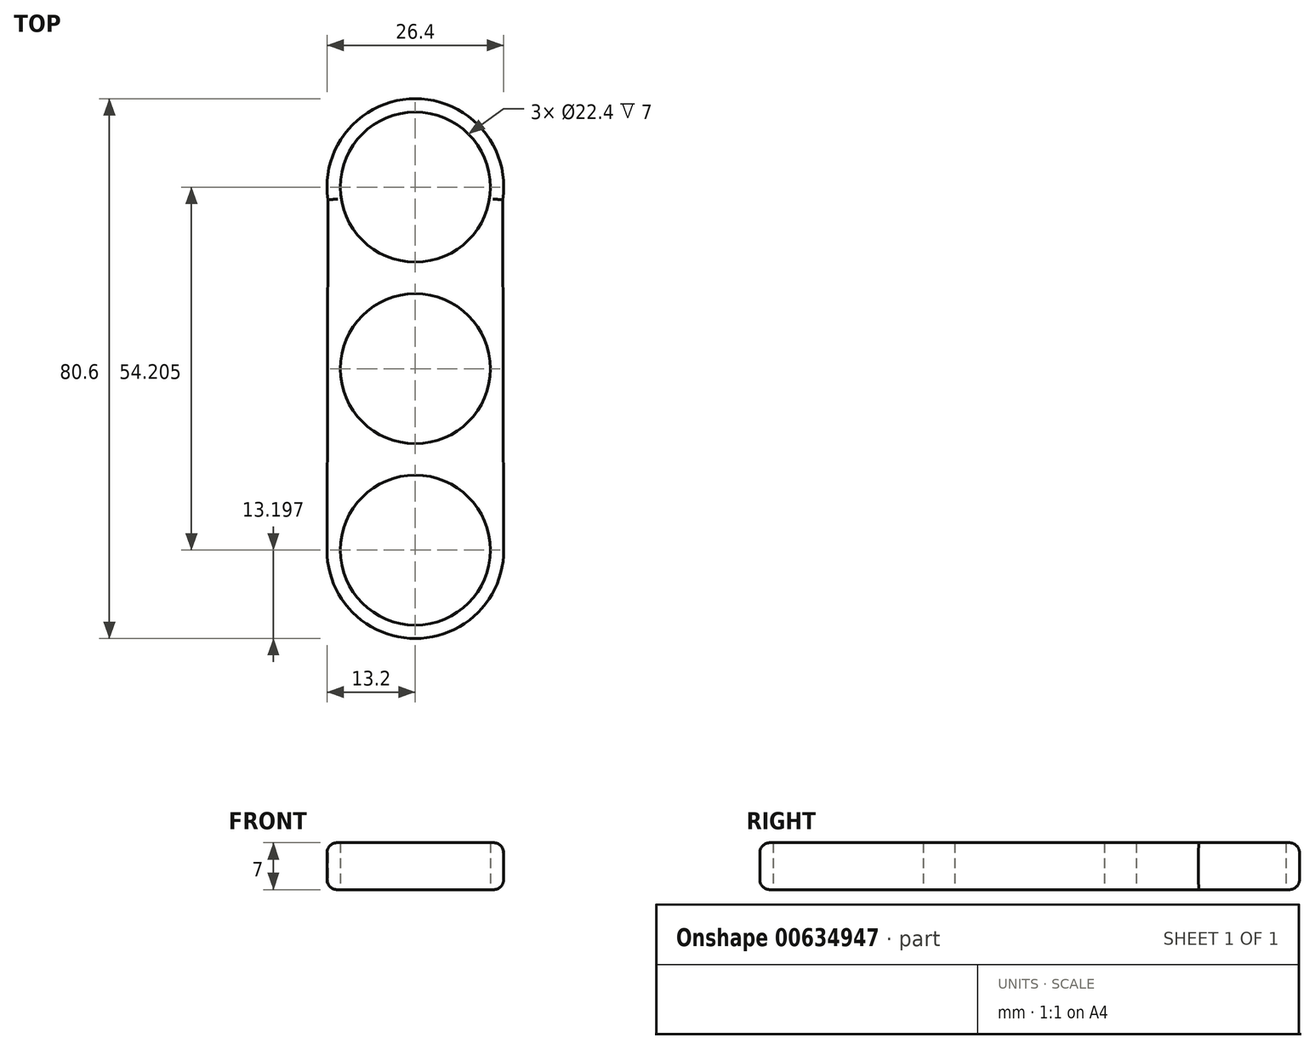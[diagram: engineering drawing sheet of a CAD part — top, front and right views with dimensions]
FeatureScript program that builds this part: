
annotation { "Feature Type Name" : "Feature", "Feature Type Description" : "" }
export const myFeature = defineFeature(function(context is Context, id is Id, definition is map)
    precondition{}
    {
        {
            var Q0;
            Q0=qCreatedBy(makeId("Top.planeOp"),FACE);
            var sketch = newSketch(context, id + "F0", { "sketchPlane" : qUnion([Q0])});
            skCircle(sketch, "E0", {"center": v(0, 0) * mm, "radius": 11.2 * mm});
            skArc(sketch, "E1", {"start": v(13.13, -1.33) * mm, "mid": v(13.2, 0.03) * mm, "end": v(13.13, 1.4) * mm});
            skCircle(sketch, "E2", {"center": v(0, 27.12) * mm, "radius": 11.2 * mm});
            skArc(sketch, "E3", {"start": v(13.06, 25.23) * mm, "mid": v(0, 40.32) * mm, "end": v(-13.06, 25.23) * mm});
            skCircle(sketch, "E4.1.0", {"center": v(0, -27.08) * mm, "radius": 11.2 * mm});
            skArc(sketch, "E4.1.1", {"start": v(-13.2, -27.05) * mm, "mid": v(0, -40.28) * mm, "end": v(13.2, -27.05) * mm});
            skPoint(sketch, "E4.center", {"position": v(0, 0.02) * mm});
            skLineSegment(sketch, "E5", {"start": v(13.06, 25.23) * mm, "end": v(13.2, -27.05) * mm});
            skLineSegment(sketch, "E6", {"start": v(-13.06, 25.23) * mm, "end": v(-13.2, -27.05) * mm});
            skArc(sketch, "E7.trimOffspring", {"start": v(-13.13, 1.4) * mm, "mid": v(-13.2, 0.03) * mm, "end": v(-13.13, -1.33) * mm});
            skSolve(sketch);
        }
        {
            var Q0;
            Q0=qCreatedBy(makeId("Top.planeOp"),FACE);
            var sketch = newSketch(context, id + "F1", { "sketchPlane" : qUnion([Q0])});
            skSolve(sketch);
        }
        {
            var Q0;
            Q0 = qSketchRegion(id + "F1", true);
            var Q1;
            Q1=makeQuery(id+"F0.imprint","IMPRINT",FACE,{"disambiguationData":[TD([[makeQuery(id+"F0.imprint","IMPRINT",EDGE,{"derivedFrom":sQuery(id+"F0.wireOp",EDGE,"E0")}),-1.0]])]});
            extrude(context, id + "F2", {"entities" : qUnion([Q0, Q1]), "depth" : 7 * mm, "offsetDistance" : 25 * mm});
        }
        {
            var Q0;
            Q0=makeQuery(id+"F2.opExtrude","CAP_EDGE",EDGE,{"disambiguationData":[OSD([sQuery(id+"F0.wireOp",EDGE,"E5")])],"isStart":false});
            var Q1;
            Q1=makeQuery(id+"F2.opExtrude","CAP_EDGE",EDGE,{"disambiguationData":[OSD([sQuery(id+"F0.wireOp",EDGE,"E4.1.1")])],"isStart":false});
            var Q2;
            Q2=makeQuery(id+"F2.opExtrude","CAP_EDGE",EDGE,{"disambiguationData":[OSD([sQuery(id+"F0.wireOp",EDGE,"E6")])],"isStart":false});
            var Q3;
            Q3=makeQuery(id+"F2.opExtrude","CAP_EDGE",EDGE,{"disambiguationData":[OSD([sQuery(id+"F0.wireOp",EDGE,"E3")])],"isStart":false});
            fillet(context, id + "F3", {"entities" : qUnion([Q0, Q1, Q2, Q3]), "radius" : 1.5 * mm, "tangentPropagation" : true, "allowEdgeOverflow" : false});
        }
        {
            var Q0;
            Q0=makeQuery(id+"F2.opExtrude","CAP_EDGE",EDGE,{"disambiguationData":[OSD([sQuery(id+"F0.wireOp",EDGE,"E3")])],"isStart":true});
            var Q1;
            Q1=makeQuery(id+"F2.opExtrude","CAP_EDGE",EDGE,{"disambiguationData":[OSD([sQuery(id+"F0.wireOp",EDGE,"E5")])],"isStart":true});
            var Q2;
            Q2=makeQuery(id+"F2.opExtrude","CAP_EDGE",EDGE,{"disambiguationData":[OSD([sQuery(id+"F0.wireOp",EDGE,"E6")])],"isStart":true});
            var Q3;
            Q3=makeQuery(id+"F2.opExtrude","CAP_EDGE",EDGE,{"disambiguationData":[OSD([sQuery(id+"F0.wireOp",EDGE,"E4.1.1")])],"isStart":true});
            fillet(context, id + "F4", {"entities" : qUnion([Q0, Q1, Q2, Q3]), "radius" : 1.5 * mm, "tangentPropagation" : true, "allowEdgeOverflow" : false});
        }
    });
